# Revit family: klemmstück
name_source: partatom
category: Generic Models
revit_build: Autodesk Revit 2017 (Build: 20160225_1515(x64)
units: mm (PartAtom-declared; Revit-internal decimal feet)

## family parameters
Always vertical = Yes
Can host rebar = No
Cut with Voids When Loaded = No
Part Type = Normal
Room Calculation Point = No
Round Connector Dimension = Use Diameter
Shared = No
Work Plane-Based = No

## types (6) — shared parameters
Manufacturer = OBO BETTERMANN
URL = http://www.obo-bettermann.com

## per-type parameters (varying)
| type | GTIN | Manufacturer Art.No. | Material |
| GKS 34 G | 4012197261436 | 6016855 | Electro-galvanised |
| GKS 34 FS SP | 4012196120314 | 6016857 | Strip-galvanised |
| GKS 34 FT | 4012196013395 | 6016820 | Hot-dip galvanised |
| GKS 34 A2 | 4012196013456 | 6016839 | Stainless steel, A2 |
| GKS 34 A4 | 4012196120437 | 6016859 | Stainless steel, A4 |
| GKS 34 FTK LGR | 4012196332533 | 6479367 | Steel |

note: column(s) folded — value = type name in every type: Article Type

## geometry (parser evidence)
native form markers: Sweep x2
no freeform markers — native parametric forms only
